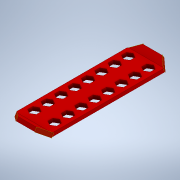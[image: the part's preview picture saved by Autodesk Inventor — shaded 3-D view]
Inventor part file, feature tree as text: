
AUTODESK INVENTOR PART (.ipt)
format: ipt  version: 2020 (Build 240168000, 168)  size: 468,992 bytes
history: native  units: in
note: dims shown in document units (in); Inventor stores cm internally (conversion verified against a paired STEP export)
features: extrude x7, sketch x7, other x4, plane x4
ambient origin geometry x8: Origin, YZ Plane, XZ Plane, XY Plane, X Axis, Y Axis, Z Axis, Center Point
bodies: Solid1 (feature_tree)
feature tree (22):
  other  "HexFlipper.ipt"
  extrude  "Extrusion1"  Depth=0.0787in TaperAngle=0.0deg
  extrude  "Extrusion2"  Depth=0.0787in TaperAngle=0.0deg
  extrude  "Extrusion3"  TaperAngle=135.0deg  [1 undecoded]
  plane  "Work Plane1"
  extrude  "Extrusion4"  Depth=0.9518in TaperAngle=0.0deg
  plane  "Work Plane2"
  extrude  "Extrusion5"  TaperAngle=135.0deg  [1 undecoded]
  plane  "Work Plane3"
  extrude  "Extrusion6"  TaperAngle=0.0deg  [1 undecoded]
  plane  "Work Plane4"
  extrude  "Extrusion7"  [1 undecoded]
  other  "TaggingFeature1"
  sketch  "Sketch1"  dims[d0=0.3937in d1=0.0787in d2=0.0in]
  sketch  "Sketch2"  dims[d3=0.0787in d4=0.0in d5=0.0787in d6=0.0in]
  sketch  "Sketch3"  dims[d7=45.0deg d8=135.0deg]
  sketch  "Sketch4"  dims[d9=0.8199in d10=0.0in d11=0.9518in d12=0.0in]
  sketch  "Sketch5"  dims[d13=45.0deg d14=135.0deg]
  sketch  "Sketch6"  dims[d15=0.0in d16=0.0in d17=0.0in d18=0.0in]
  sketch  "Sketch7"
  other  "Solid1::HexFlipper.ipt"
  other  "Srf1"
note: 4 required parameter values undecoded (feature->parameter linkage not recoverable at this tier; creation-order binding heuristic only, values carry confidence <= 0.55)
